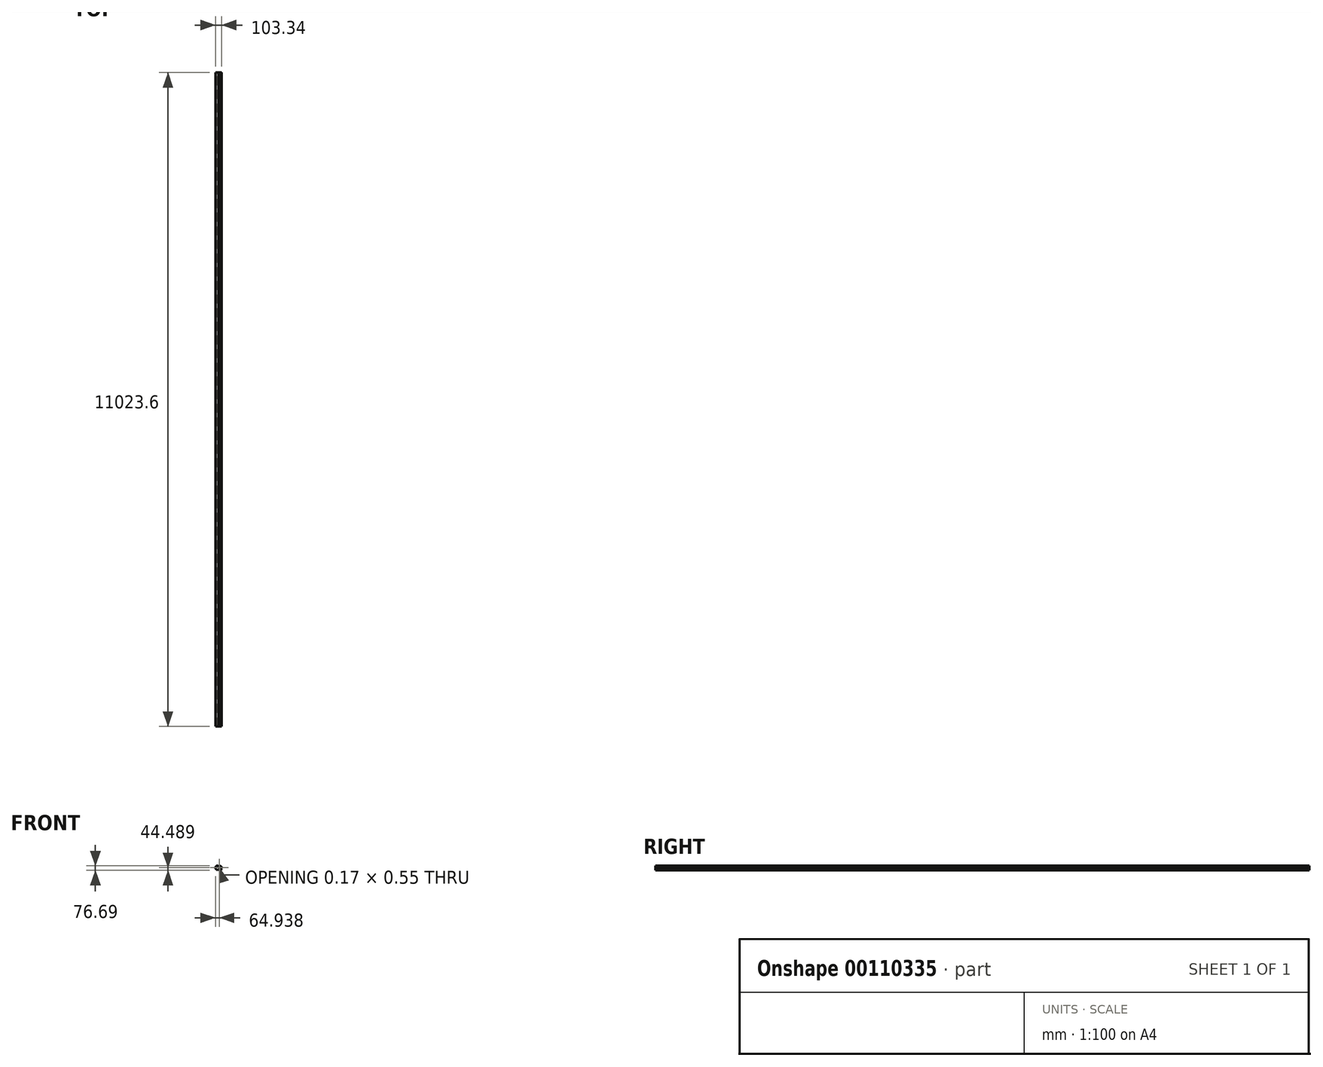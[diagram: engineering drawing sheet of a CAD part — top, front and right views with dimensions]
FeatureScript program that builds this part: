
annotation { "Feature Type Name" : "Feature", "Feature Type Description" : "" }
export const myFeature = defineFeature(function(context is Context, id is Id, definition is map)
    precondition{}
    {
        {
            var Q0;
            Q0=qCreatedBy(makeId("Front.planeOp"),FACE);
            var sketch = newSketch(context, id + "F0", { "sketchPlane" : qUnion([Q0])});
            skArc(sketch, "E0", {"start": v(12, 17.18) * mm, "mid": v(12.08, 16.95) * mm, "end": v(12.16, 16.72) * mm});
            skArc(sketch, "E1", {"start": v(28.93, 43.78) * mm, "mid": v(14.85, 46.81) * mm, "end": v(1.99, 40.31) * mm});
            skArc(sketch, "E2", {"start": v(12.16, 17.27) * mm, "mid": v(12.08, 17.23) * mm, "end": v(12, 17.18) * mm});
            skArc(sketch, "E3", {"start": v(12.16, 16.72) * mm, "mid": v(12.16, 17) * mm, "end": v(12.16, 17.27) * mm});
            skArc(sketch, "E4", {"start": v(-33.37, -13.1) * mm, "mid": v(-18.03, -22.25) * mm, "end": v(-3.88, -11.35) * mm});
            skArc(sketch, "E5.trimOffspring", {"start": v(43.7, 9.06) * mm, "mid": v(48.9, 31.77) * mm, "end": v(28.93, 43.78) * mm});
            skArc(sketch, "E6.trimOffspring", {"start": v(0.21, -8.5) * mm, "mid": v(32.47, -25.75) * mm, "end": v(43.7, 9.06) * mm});
            skArc(sketch, "E7.trimOffspring", {"start": v(1.99, 40.31) * mm, "mid": v(-47.45, 34.63) * mm, "end": v(-33.37, -13.1) * mm});
            skArc(sketch, "E8.trimOffspring", {"start": v(-3.88, -11.35) * mm, "mid": v(-1.78, -10) * mm, "end": v(0.21, -8.5) * mm});
            skSolve(sketch);
        }
        {
            var Q0;
            Q0=makeQuery(id+"F0.imprint","IMPRINT",FACE,{"disambiguationData":[TD([[makeQuery(id+"F0.imprint","IMPRINT",EDGE,{"derivedFrom":sQuery(id+"F0.wireOp",EDGE,"E0")}),-1.0]])]});
            extrude(context, id + "F1", {"entities" : qUnion([Q0]), "depth" : 11023.6 * mm});
        }
    });
